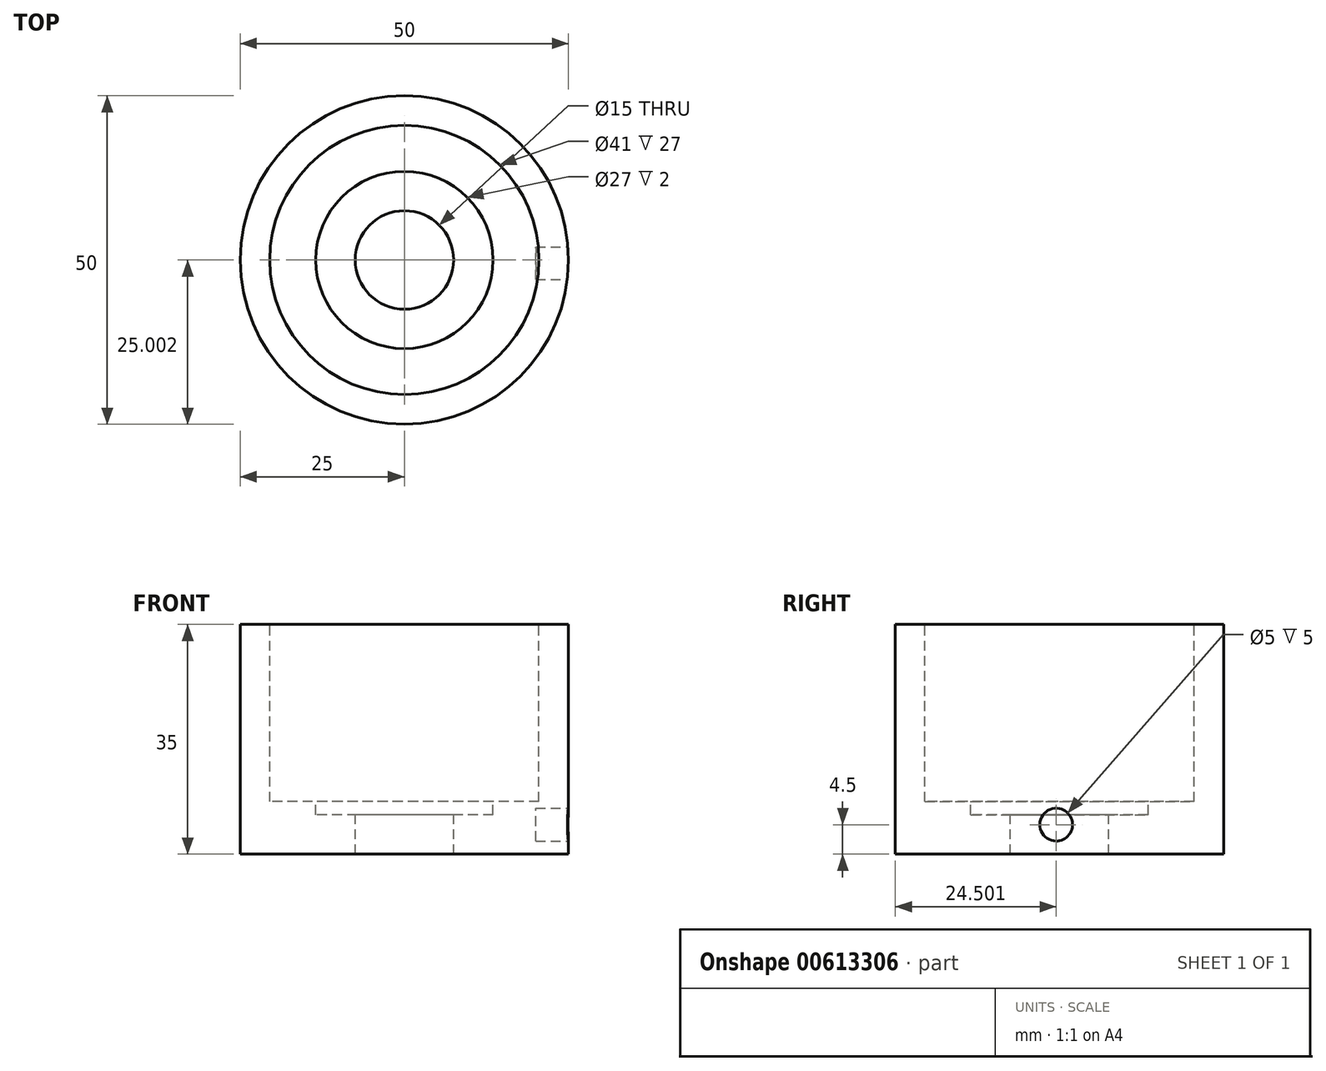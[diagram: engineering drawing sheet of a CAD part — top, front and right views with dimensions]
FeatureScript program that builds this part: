
annotation { "Feature Type Name" : "Feature", "Feature Type Description" : "" }
export const myFeature = defineFeature(function(context is Context, id is Id, definition is map)
    precondition{}
    {
        {
            var Q0;
            Q0=qCreatedBy(makeId("Top.planeOp"),FACE);
            var sketch = newSketch(context, id + "F0", { "sketchPlane" : qUnion([Q0])});
            skCircle(sketch, "E0", {"center": v(0, 6.57) * mm, "radius": 25 * mm});
            skSolve(sketch);
        }
        {
            var Q0;
            Q0=makeQuery(id+"F0.imprint","IMPRINT",FACE,{"disambiguationData":[TD([[makeQuery(id+"F0.imprint","IMPRINT",EDGE,{"derivedFrom":sQuery(id+"F0.wireOp",EDGE,"E0")}),1.0]])]});
            extrude(context, id + "F1", {"entities" : qUnion([Q0]), "depth" : 35 * mm, "offsetDistance" : 25 * mm});
        }
        {
            var Q0;
            Q0=makeQuery(id+"F1.opExtrude","CAP_FACE",FACE,{"disambiguationData":[OSD([sQuery(id+"F0.wireOp",EDGE,"E0")])],"isStart":false});
            var sketch = newSketch(context, id + "F2", { "sketchPlane" : qUnion([Q0])});
            skCircle(sketch, "E1", {"center": v(0, 6.57) * mm, "radius": 20.5 * mm});
            skSolve(sketch);
        }
        {
            var Q0;
            Q0 = qSketchRegion(id + "F2", true);
            extrude(context, id + "F3", {"entities" : qUnion([Q0]), "operationType" : NewBodyOperationType.REMOVE, "oppositeDirection" : true, "depth" : 27 * mm, "offsetDistance" : 25 * mm});
        }
        {
            var Q0;
            Q0=makeQuery(id+"F3.boolean.opBoolean","COPY",FACE,{"derivedFrom":makeQuery(id+"F3.opExtrude","CAP_FACE",FACE,{"disambiguationData":[OSD([sQuery(id+"F2.wireOp",EDGE,"E1")])],"isStart":false})});
            var sketch = newSketch(context, id + "F4", { "sketchPlane" : qUnion([Q0])});
            skCircle(sketch, "E2", {"center": v(0, 6.57) * mm, "radius": 7.5 * mm});
            skSolve(sketch);
        }
        {
            var Q0;
            Q0 = qSketchRegion(id + "F4", true);
            extrude(context, id + "F5", {"entities" : qUnion([Q0]), "operationType" : NewBodyOperationType.REMOVE, "endBound" : BoundingType.THROUGH_ALL, "oppositeDirection" : true, "depth" : 25 * mm, "offsetDistance" : 25 * mm});
        }
        {
            var Q0;
            Q0=makeQuery(id+"F3.boolean.opBoolean","COPY",FACE,{"derivedFrom":makeQuery(id+"F3.opExtrude","CAP_FACE",FACE,{"disambiguationData":[OSD([sQuery(id+"F2.wireOp",EDGE,"E1")])],"isStart":false})});
            var sketch = newSketch(context, id + "F6", { "sketchPlane" : qUnion([Q0])});
            skCircle(sketch, "E3", {"center": v(0, 6.57) * mm, "radius": 13.5 * mm});
            skSolve(sketch);
        }
        {
            var Q0;
            Q0 = qSketchRegion(id + "F6", true);
            extrude(context, id + "F7", {"entities" : qUnion([Q0]), "operationType" : NewBodyOperationType.REMOVE, "oppositeDirection" : true, "depth" : 2 * mm, "offsetDistance" : 25 * mm});
        }
        {
            var Q0;
            Q0=qCreatedBy(makeId("Front.planeOp"),FACE);
            cPlane(context, id + "F8", {"entities" : qUnion([Q0]), "cplaneType" : CPlaneType.OFFSET, "offset" : 6.07 * mm, "oppositeDirection" : true, "width" : 150 * mm, "height" : 150 * mm});
        }
        {
            var Q0;
            Q0=qCreatedBy(makeId("Right.planeOp"),FACE);
            cPlane(context, id + "F9", {"entities" : qUnion([Q0]), "cplaneType" : CPlaneType.OFFSET, "offset" : 25 * mm, "width" : 150 * mm, "height" : 150 * mm});
        }
        {
            var Q0;
            Q0=qCreatedBy(id+"F9.planeOp",FACE);
            var sketch = newSketch(context, id + "F10", { "sketchPlane" : qUnion([Q0])});
            skCircle(sketch, "E4", {"center": v(6.07, 4.5) * mm, "radius": 2.5 * mm});
            skSolve(sketch);
        }
        {
            var Q0;
            Q0 = qSketchRegion(id + "F10", true);
            extrude(context, id + "F11", {"entities" : qUnion([Q0]), "operationType" : NewBodyOperationType.REMOVE, "oppositeDirection" : true, "depth" : 5 * mm, "offsetDistance" : 25 * mm});
        }
    });
